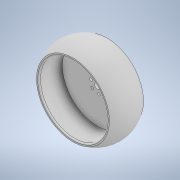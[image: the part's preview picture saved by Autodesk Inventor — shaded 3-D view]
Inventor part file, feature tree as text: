
AUTODESK INVENTOR PART (.ipt)
format: ipt  version: 2020 (Build 240168000, 168)  size: 215,552 bytes
history: native  units: mm
features: sketch x5, other x4, extrude x3, reference x2, sweep x1, shell x1, fillet x1, projected_geometry x1
ambient origin geometry x8: Origin, YZ Plane, XZ Plane, XY Plane, X Axis, Y Axis, Z Axis, Center Point
bodies: Solid1 (feature_tree)
feature tree (18):
  sweep  "Sweep1"
  shell  "Shell1"  Thickness=12.0mm
  extrude  "Extrusion1"  Depth=15.0mm
  extrude  "Extrusion2"  Depth=2.5mm
  extrude  "Extrusion3"  Depth=10.0mm
  fillet  "Fillet1"  Radius=10.0mm
  sketch  "Sketch1"  dims[d0=75.0mm d1=50.0mm d2=12.0mm]
  sketch  "Sketch2"  dims[d3=30.0mm d4=15.0mm]
  sketch  "Sketch4"  dims[d5=0.0mm d6=0.0mm d7=2.5mm]
  reference  "Reference1"
  reference  "Reference2"
  sketch  "Sketch6"  dims[d8=10.0mm d9=0.0mm d10=5.0mm d11=10.0mm d12=0.0mm]
  sketch  "Sketch7"  dims[d13=6.0mm d14=0.0mm d15=1.0mm]
  projected_geometry  "Projected Loop1"
  other  "<userpath>\Desktop\KangKangBalancing\KangKang.iam"
  other  "KangKang.iam"
  other  "tarot_5008_340kv_assy:1"
  other  "housing0:1"
